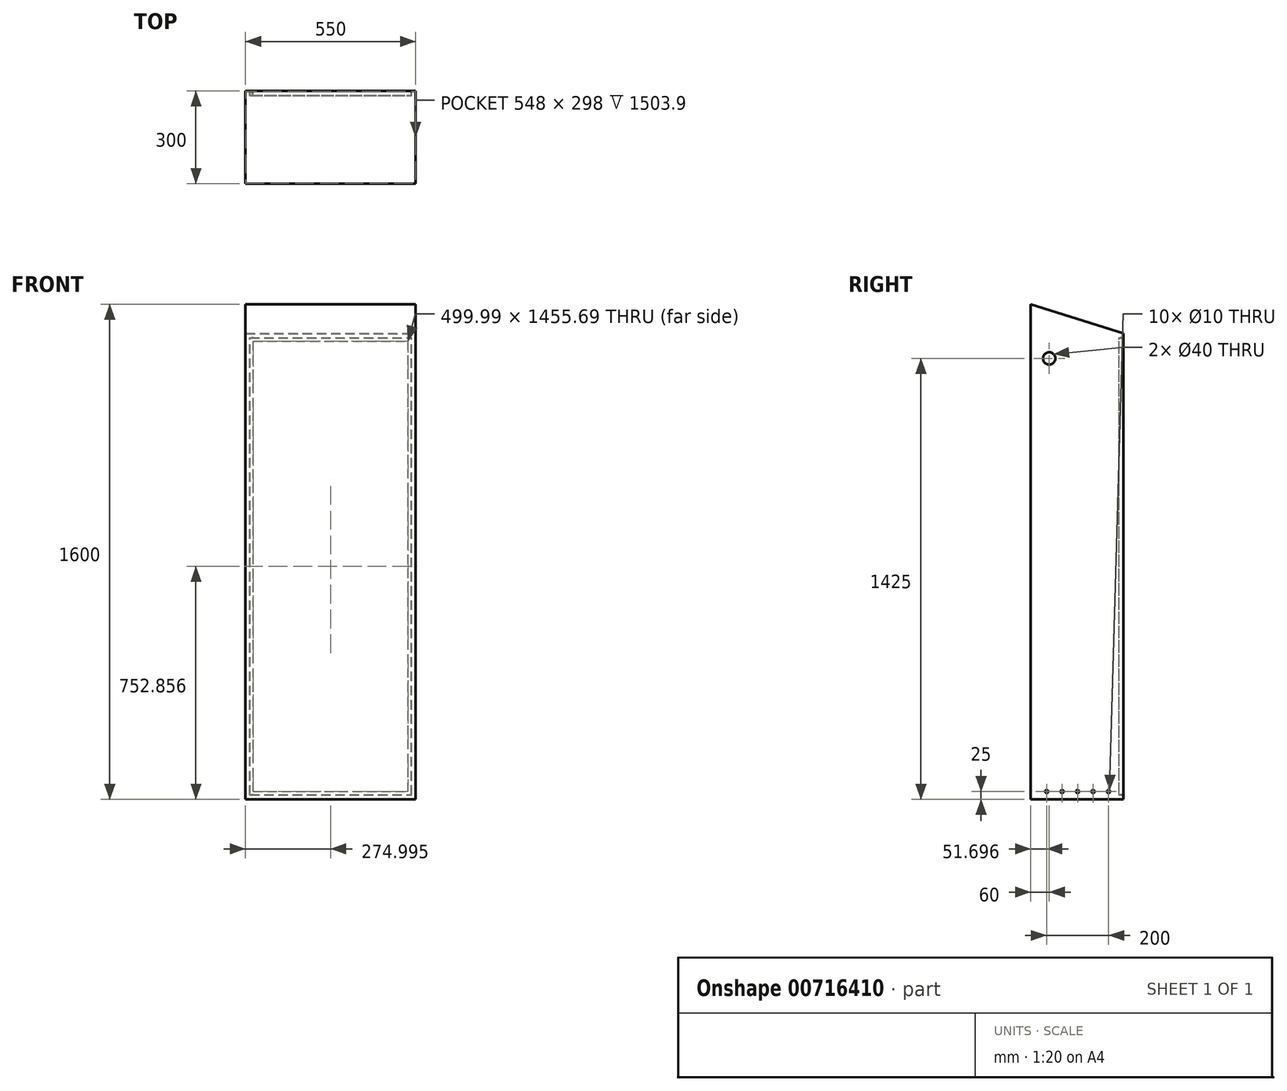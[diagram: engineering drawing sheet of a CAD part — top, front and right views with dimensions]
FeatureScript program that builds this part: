
annotation { "Feature Type Name" : "Feature", "Feature Type Description" : "" }
export const myFeature = defineFeature(function(context is Context, id is Id, definition is map)
    precondition{}
    {
        {
            var Q0;
            Q0=qCreatedBy(makeId("Top.planeOp"),FACE);
            var sketch = newSketch(context, id + "F0", { "sketchPlane" : qUnion([Q0])});
            skLineSegment(sketch, "E0.bottom", {"start": v(0, 0) * mm, "end": v(550, 0) * mm});
            skLineSegment(sketch, "E0.top", {"start": v(0, 300) * mm, "end": v(550, 300) * mm});
            skLineSegment(sketch, "E0.left", {"start": v(0, 0) * mm, "end": v(0, 300) * mm});
            skLineSegment(sketch, "E0.right", {"start": v(550, 0) * mm, "end": v(550, 300) * mm});
            skSolve(sketch);
        }
        {
            var Q0;
            Q0=qSketchRegion(id+"F0",true);
            extrude(context, id + "F1", {"entities" : qUnion([Q0]), "depth" : 1600 * mm, "offsetDistance" : 25 * mm});
        }
        {
            var Q0;
            Q0=makeQuery(id+"F1.opExtrude","SWEPT_FACE",FACE,{"disambiguationData":[OSD([sQuery(id+"F0.wireOp",EDGE,"E0.right")])]});
            var sketch = newSketch(context, id + "F2", { "sketchPlane" : qUnion([Q0])});
            skLineSegment(sketch, "E1", {"start": v(0, 1600) * mm, "end": v(300, 1505.63) * mm});
            skLineSegment(sketch, "E2", {"start": v(300, 1505.63) * mm, "end": v(300, 1600) * mm});
            skLineSegment(sketch, "E3", {"start": v(300, 1600) * mm, "end": v(0, 1600) * mm});
            skSolve(sketch);
        }
        {
            var Q0;
            Q0 = qSketchRegion(id + "F2", true);
            extrude(context, id + "F3", {"entities" : qUnion([Q0]), "operationType" : NewBodyOperationType.REMOVE, "endBound" : BoundingType.THROUGH_ALL, "oppositeDirection" : true, "depth" : 25 * mm, "offsetDistance" : 25 * mm});
        }
        {
            var Q0;
            Q0=makeQuery(id+"F1.opExtrude","SWEPT_FACE",FACE,{"disambiguationData":[OSD([sQuery(id+"F0.wireOp",EDGE,"E0.top")])]});
            var sketch = newSketch(context, id + "F4", { "sketchPlane" : qUnion([Q0])});
            skLineSegment(sketch, "E4.bottom", {"start": v(-15, 15) * mm, "end": v(-535, 15) * mm});
            skLineSegment(sketch, "E4.top", {"start": v(-15, 1490.63) * mm, "end": v(-535, 1490.63) * mm});
            skLineSegment(sketch, "E4.left", {"start": v(-15, 15) * mm, "end": v(-15, 1490.63) * mm});
            skLineSegment(sketch, "E4.right", {"start": v(-535, 15) * mm, "end": v(-535, 1490.63) * mm});
            skSolve(sketch);
        }
        {
            var Q0;
            Q0 = qSketchRegion(id + "F4", true);
            extrude(context, id + "F5", {"entities" : qUnion([Q0]), "operationType" : NewBodyOperationType.REMOVE, "oppositeDirection" : true, "depth" : 15 * mm, "offsetDistance" : 25 * mm});
        }
        {
            var Q0;
            Q0=makeQuery(id+"F5.boolean.opBoolean","COPY",FACE,{"derivedFrom":makeQuery(id+"F5.opExtrude","CAP_FACE",FACE,{"disambiguationData":[OSD([sQuery(id+"F4.wireOp",EDGE,"E4.bottom"),sQuery(id+"F4.wireOp",EDGE,"E4.top"),sQuery(id+"F4.wireOp",EDGE,"E4.left"),sQuery(id+"F4.wireOp",EDGE,"E4.right")])],"isStart":false})});
            shell(context, id + "F6", {"entities" : qUnion([Q0]), "thickness" : 1 * mm});
        }
        {
            var Q0;
            Q0=qCreatedBy(makeId("Front.planeOp"),FACE);
            cPlane(context, id + "F7", {"entities" : qUnion([Q0]), "cplaneType" : CPlaneType.OFFSET, "offset" : 285 * mm, "oppositeDirection" : true, "width" : 150 * mm, "height" : 150 * mm});
        }
        {
            var Q0;
            Q0=qCreatedBy(id+"F7.planeOp",FACE);
            var sketch = newSketch(context, id + "F8", { "sketchPlane" : qUnion([Q0])});
            skLineSegment(sketch, "E5.bottom", {"start": v(15, 15) * mm, "end": v(535, 15) * mm});
            skLineSegment(sketch, "E5.top", {"start": v(15, 1490.7) * mm, "end": v(535, 1490.7) * mm});
            skLineSegment(sketch, "E5.left", {"start": v(15, 15) * mm, "end": v(15, 1490.7) * mm});
            skLineSegment(sketch, "E5.right", {"start": v(535, 15) * mm, "end": v(535, 1490.7) * mm});
            skLineSegment(sketch, "E6.0", {"start": v(25, 25) * mm, "end": v(25, 1480.7) * mm});
            skLineSegment(sketch, "E6.1", {"start": v(25, 25) * mm, "end": v(525, 25) * mm});
            skLineSegment(sketch, "E6.2", {"start": v(525, 25) * mm, "end": v(525, 1480.7) * mm});
            skLineSegment(sketch, "E6.3", {"start": v(25, 1480.7) * mm, "end": v(525, 1480.7) * mm});
            skSolve(sketch);
        }
        {
            var Q0;
            Q0 = qSketchRegion(id + "F8", true);
            extrude(context, id + "F9", {"entities" : qUnion([Q0]), "operationType" : NewBodyOperationType.ADD, "oppositeDirection" : true, "depth" : 1 * mm, "offsetDistance" : 25 * mm});
        }
        {
            var Q0;
            Q0=makeQuery(id+"F5.boolean.opBoolean","COPY",FACE,{"derivedFrom":makeQuery(id+"F5.opExtrude","SWEPT_FACE",FACE,{"disambiguationData":[OSD([sQuery(id+"F4.wireOp",EDGE,"E4.bottom")])]})});
            var sketch = newSketch(context, id + "F10", { "sketchPlane" : qUnion([Q0])});
            skCircle(sketch, "E7", {"center": v(22.23, 293) * mm, "radius": 3 * mm});
            skSolve(sketch);
        }
        {
            var Q0;
            Q0 = qSketchRegion(id + "F10", true);
            var Q1;
            Q1=makeQuery(id+"F5.boolean.opBoolean","COPY",FACE,{"derivedFrom":makeQuery(id+"F5.opExtrude","SWEPT_FACE",FACE,{"disambiguationData":[OSD([sQuery(id+"F4.wireOp",EDGE,"E4.top")])]})});
            var Q2;
            Q2=makeQuery(id+"F1.opExtrude","SWEPT_BODY",BODY,{"disambiguationData":[OSD([sQuery(id+"F0.wireOp",EDGE,"E0.bottom"),sQuery(id+"F0.wireOp",EDGE,"E0.top"),sQuery(id+"F0.wireOp",EDGE,"E0.left"),sQuery(id+"F0.wireOp",EDGE,"E0.right")])]});
            extrude(context, id + "F11", {"entities" : qUnion([Q0]), "operationType" : NewBodyOperationType.REMOVE, "oppositeDirection" : true, "depth" : 5 * mm, "offsetDistance" : 25 * mm, "hasSecondDirection" : true, "secondDirectionOppositeDirection" : false, "secondDirectionDepth" : 1490 * mm, "secondDirectionBoundEntityFace" : qUnion([Q1]), "secondDirectionBoundEntityBody" : qUnion([Q2])});
        }
        {
            var Q0;
            Q0=makeQuery(id+"F1.opExtrude","SWEPT_FACE",FACE,{"disambiguationData":[OSD([sQuery(id+"F0.wireOp",EDGE,"E0.right")])]});
            var sketch = newSketch(context, id + "F12", { "sketchPlane" : qUnion([Q0])});
            skLineSegment(sketch, "E8", {"start": v(0, 25) * mm, "end": v(300, 25) * mm, "construction": true});
            skLineSegment(sketch, "E9", {"start": v(0, 144.52) * mm, "end": v(300, 144.52) * mm, "construction": true});
            skCircle(sketch, "E10", {"center": v(51.7, 25) * mm, "radius": 5 * mm});
            skCircle(sketch, "E11.1.0.0", {"center": v(101.7, 25) * mm, "radius": 5 * mm});
            skCircle(sketch, "E11.2.0.0", {"center": v(151.7, 25) * mm, "radius": 5 * mm});
            skCircle(sketch, "E11.3.0.0", {"center": v(201.7, 25) * mm, "radius": 5 * mm});
            skCircle(sketch, "E11.4.0.0", {"center": v(251.7, 25) * mm, "radius": 5 * mm});
            skLineSegment(sketch, "E11.direction1", {"start": v(51.7, 25) * mm, "end": v(101.7, 25) * mm, "construction": true});
            skSolve(sketch);
        }
        {
            var Q0;
            Q0 = qSketchRegion(id + "F12", true);
            extrude(context, id + "F13", {"entities" : qUnion([Q0]), "operationType" : NewBodyOperationType.REMOVE, "endBound" : BoundingType.THROUGH_ALL, "oppositeDirection" : true, "depth" : 25 * mm, "offsetDistance" : 25 * mm});
        }
        {
            var Q0;
            Q0=makeQuery(id+"F1.opExtrude","SWEPT_FACE",FACE,{"disambiguationData":[OSD([sQuery(id+"F0.wireOp",EDGE,"E0.left")])]});
            var sketch = newSketch(context, id + "F14", { "sketchPlane" : qUnion([Q0])});
            skCircle(sketch, "E12", {"center": v(-60, 1425) * mm, "radius": 20 * mm});
            skSolve(sketch);
        }
        {
            var Q0;
            Q0 = qSketchRegion(id + "F14", true);
            extrude(context, id + "F15", {"entities" : qUnion([Q0]), "operationType" : NewBodyOperationType.REMOVE, "endBound" : BoundingType.THROUGH_ALL, "oppositeDirection" : true, "depth" : 25 * mm, "offsetDistance" : 25 * mm});
        }
    });
